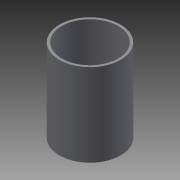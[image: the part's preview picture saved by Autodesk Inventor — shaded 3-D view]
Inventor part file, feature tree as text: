
AUTODESK INVENTOR PART (.ipt)
format: ipt  version: 2014 SP2 (Build 180246200, 246)  size: 120,832 bytes
history: native  units: in
note: dims shown in document units (in); Inventor stores cm internally (conversion verified against a paired STEP export)
features: other x84, revolve x1, sketch x1
ambient origin geometry x8: Origin, YZ Plane, XZ Plane, XY Plane, X Axis, Y Axis, Z Axis, Center Point
bodies: Solid1 (feature_tree)
feature tree (86):
  revolve  "Revolution1"  [1 undecoded]
  other  "rod_to_part_XY"
  other  "rod_to_part_YZ"
  other  "rod_to_part_ZX"
  other  "rod_to_part_X"
  other  "rod_to_part_Y"
  other  "rod_to_part_Z"
  other  "rod_to_part_Center"
  other  "to_road_XY"
  other  "to_road_YZ"
  other  "to_road_ZX"
  other  "to_road_X"
  other  "to_road_Y"
  other  "to_road_Z"
  other  "to_road_Center"
  other  "track1_XY"
  other  "track1_YZ"
  other  "track1_ZX"
  other  "track1_X"
  other  "track1_Y"
  other  "track1_Z"
  other  "track1_Center"
  other  "track1_u_XY"
  other  "track1_u_YZ"
  other  "track1_u_ZX"
  other  "track1_u_X"
  other  "track1_u_Y"
  other  "track1_u_Z"
  other  "track1_u_Center"
  other  "track2_XY"
  other  "track2_YZ"
  other  "track2_ZX"
  other  "track2_X"
  other  "track2_Y"
  other  "track2_Z"
  other  "track2_Center"
  other  "track2_u_XY"
  other  "track2_u_YZ"
  other  "track2_u_ZX"
  other  "track2_u_X"
  other  "track2_u_Y"
  other  "track2_u_Z"
  other  "track2_u_Center"
  other  "track3_XY"
  other  "track3_YZ"
  other  "track3_ZX"
  other  "track3_X"
  other  "track3_Y"
  other  "track3_Z"
  other  "track3_Center"
  other  "track3_u_XY"
  other  "track3_u_YZ"
  other  "track3_u_ZX"
  other  "track3_u_X"
  other  "track3_u_Y"
  other  "track3_u_Z"
  other  "track3_u_Center"
  other  "track4_XY"
  other  "track4_YZ"
  other  "track4_ZX"
  other  "track4_X"
  other  "track4_Y"
  other  "track4_Z"
  other  "track4_Center"
  other  "track4_u_XY"
  other  "track4_u_YZ"
  other  "track4_u_ZX"
  other  "track4_u_X"
  other  "track4_u_Y"
  other  "track4_u_Z"
  other  "track4_u_Center"
  other  "tube_rear_XY"
  other  "tube_rear_YZ"
  other  "tube_rear_ZX"
  other  "tube_rear_X"
  other  "tube_rear_Y"
  other  "tube_rear_Z"
  other  "tube_rear_Center"
  other  "tube_rod_guide_XY"
  other  "tube_rod_guide_YZ"
  other  "tube_rod_guide_ZX"
  other  "tube_rod_guide_X"
  other  "tube_rod_guide_Y"
  other  "tube_rod_guide_Z"
  other  "tube_rod_guide_Center"
  sketch  "Sketch_4"  dims[d0=360.0deg d1=0.0in d2=0.0in]
note: 1 required parameter value undecoded (feature->parameter linkage not recoverable at this tier; creation-order binding heuristic only, values carry confidence <= 0.55)
